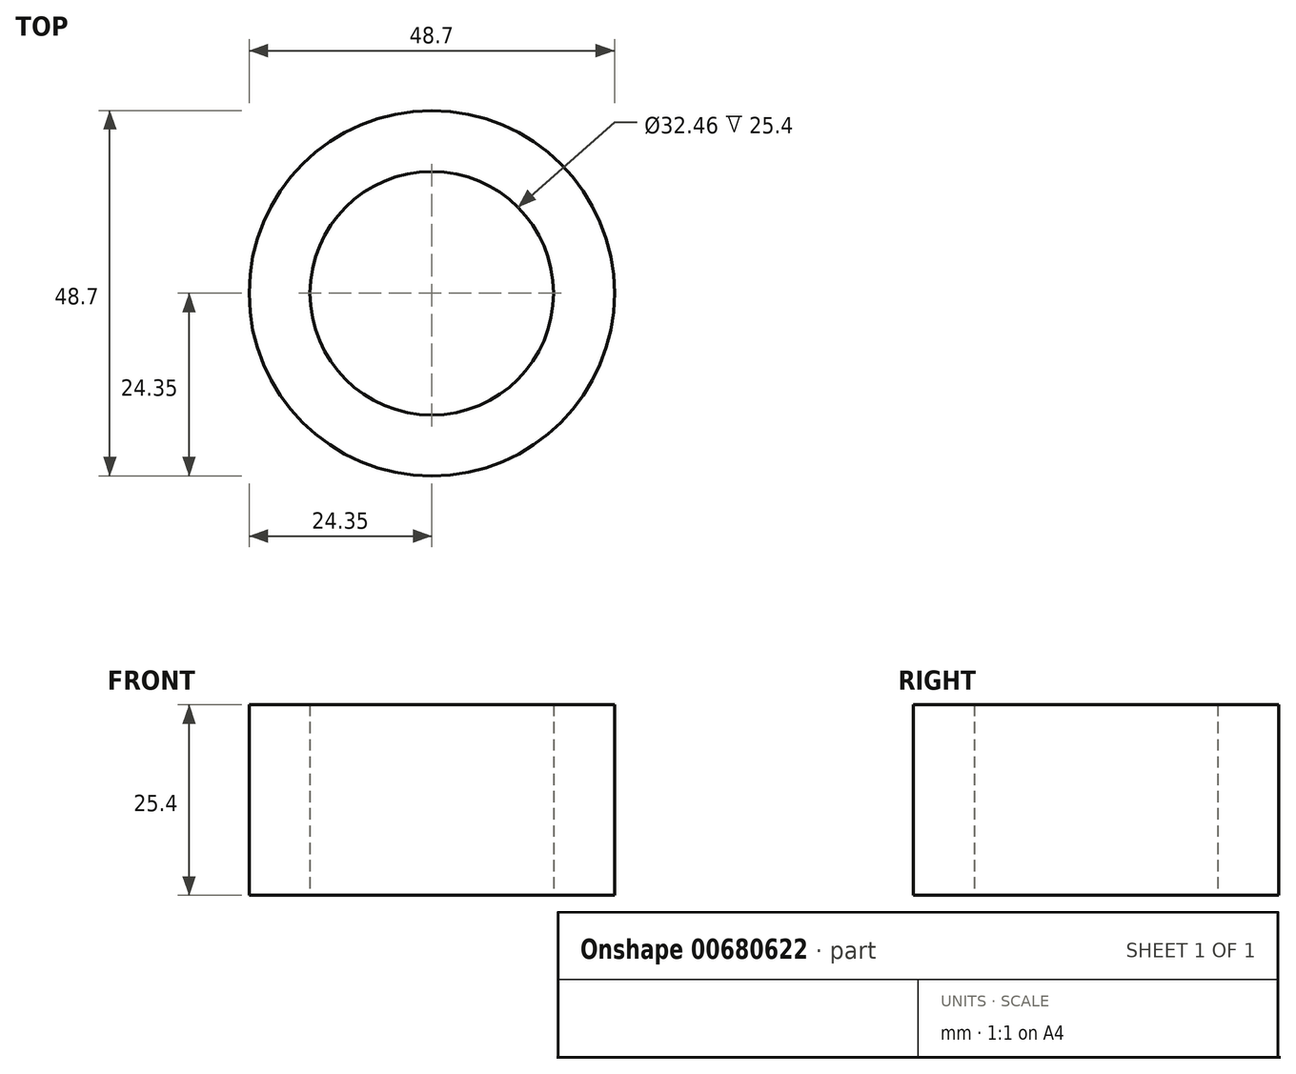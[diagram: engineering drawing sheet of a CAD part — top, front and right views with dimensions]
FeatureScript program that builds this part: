
annotation { "Feature Type Name" : "Feature", "Feature Type Description" : "" }
export const myFeature = defineFeature(function(context is Context, id is Id, definition is map)
    precondition{}
    {
        {
            var Q0;
            Q0=qCreatedBy(makeId("Top.planeOp"),FACE);
            var sketch = newSketch(context, id + "F0", { "sketchPlane" : qUnion([Q0])});
            skCircle(sketch, "E0", {"center": v(0, 0) * mm, "radius": 24.35 * mm});
            skCircle(sketch, "E1", {"center": v(0, 0) * mm, "radius": 16.23 * mm});
            skSolve(sketch);
        }
        {
            var Q0;
            Q0=makeQuery(id+"F0.imprint","IMPRINT",FACE,{"disambiguationData":[TD([[makeQuery(id+"F0.imprint","IMPRINT",EDGE,{"derivedFrom":sQuery(id+"F0.wireOp",EDGE,"E0")}),1.0]])]});
            extrude(context, id + "F1", {"entities" : qUnion([Q0]), "depth" : 25.4 * mm, "offsetDistance" : 25.4 * mm});
        }
    });
